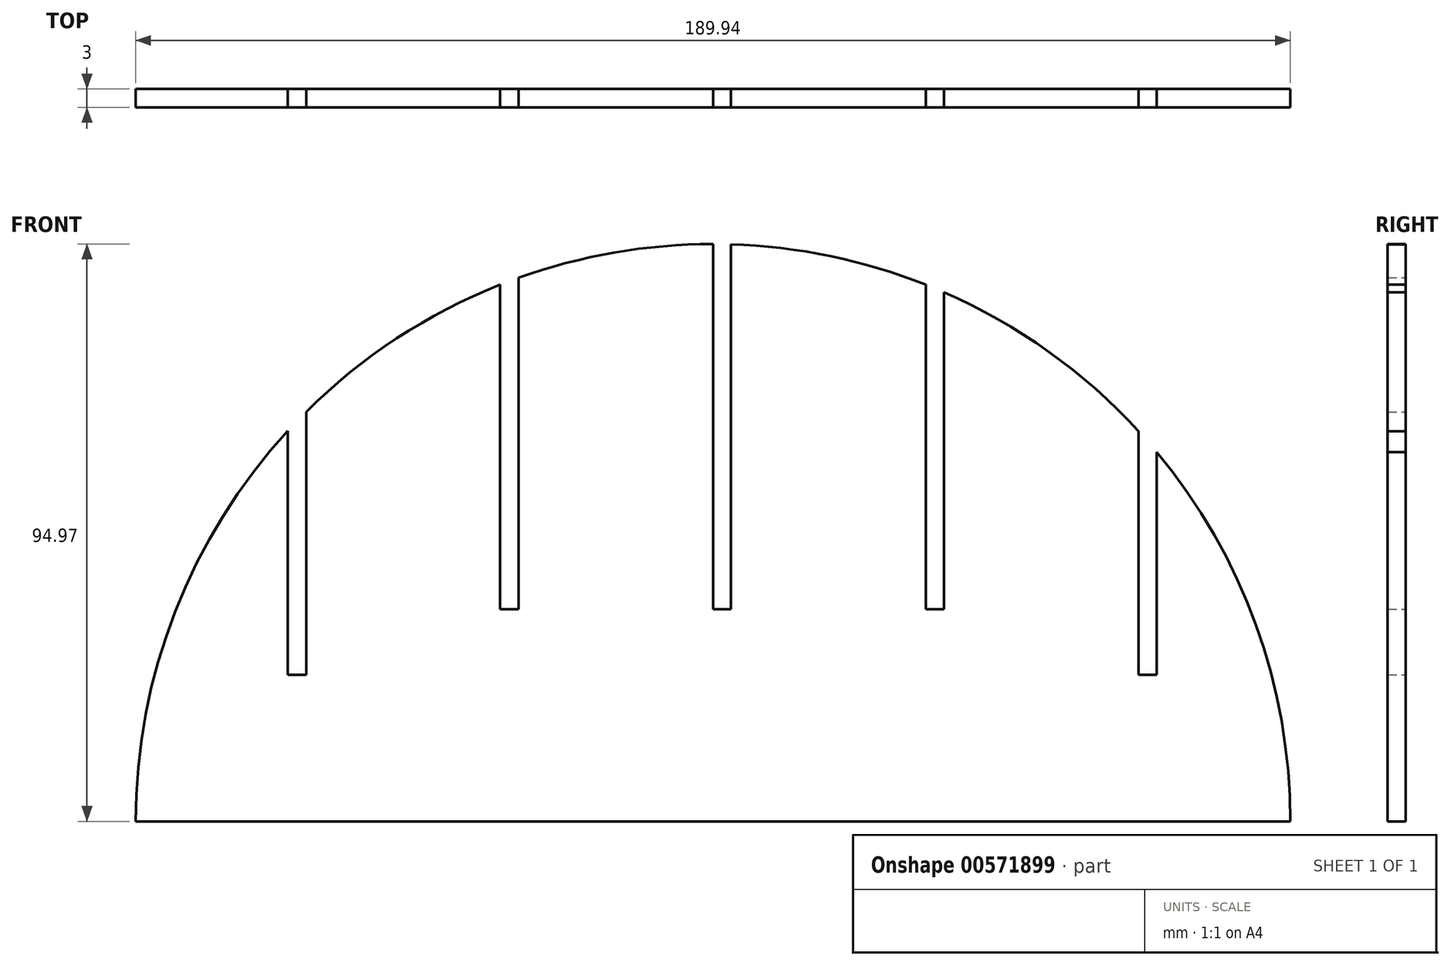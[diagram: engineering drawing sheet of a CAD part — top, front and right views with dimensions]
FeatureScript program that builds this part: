
annotation { "Feature Type Name" : "Feature", "Feature Type Description" : "" }
export const myFeature = defineFeature(function(context is Context, id is Id, definition is map)
    precondition{}
    {
        {
            var Q0;
            Q0=qCreatedBy(makeId("Front.planeOp"),FACE);
            var sketch = newSketch(context, id + "F0", { "sketchPlane" : qUnion([Q0])});
            skLineSegment(sketch, "E0", {"start": v(94.97, 0) * mm, "end": v(-95.03, 0) * mm});
            skArc(sketch, "E1", {"start": v(94.97, 0) * mm, "mid": v(89.3, 32.3) * mm, "end": v(73, 60.75) * mm});
            skLineSegment(sketch, "E2", {"start": v(-94.97, 0) * mm, "end": v(-69.93, 0) * mm});
            skLineSegment(sketch, "E3", {"start": v(94.97, 0) * mm, "end": v(70, 0) * mm});
            skLineSegment(sketch, "E4", {"start": v(-69.93, 24.1) * mm, "end": v(-69.93, 64.26) * mm});
            skLineSegment(sketch, "E5", {"start": v(-69.93, 0) * mm, "end": v(-35, 0) * mm});
            skLineSegment(sketch, "E6", {"start": v(-35, 0) * mm, "end": v(0, 0) * mm});
            skLineSegment(sketch, "E7", {"start": v(0, 0) * mm, "end": v(35, 0) * mm});
            skLineSegment(sketch, "E8", {"start": v(35, 0) * mm, "end": v(70, 0) * mm});
            skLineSegment(sketch, "E9", {"start": v(-69.93, 64.26) * mm, "end": v(-69.93, 24.1) * mm});
            skLineSegment(sketch, "E10", {"start": v(-35, 34.92) * mm, "end": v(-35, 88.28) * mm});
            skLineSegment(sketch, "E11", {"start": v(0, 34.92) * mm, "end": v(0, 94.97) * mm});
            skLineSegment(sketch, "E12", {"start": v(35, 34.92) * mm, "end": v(35, 88.28) * mm});
            skLineSegment(sketch, "E13", {"start": v(70, 24.1) * mm, "end": v(70, 64.18) * mm});
            skLineSegment(sketch, "E14", {"start": v(-35, 88.28) * mm, "end": v(-35, 34.92) * mm});
            skLineSegment(sketch, "E15", {"start": v(0, 34.92) * mm, "end": v(2.96, 34.92) * mm});
            skPoint(sketch, "E16", {"position": v(0, 34.92) * mm});
            skPoint(sketch, "E17", {"position": v(35, 34.92) * mm});
            skLineSegment(sketch, "E18", {"start": v(-69.93, 24.1) * mm, "end": v(-66.93, 24.1) * mm});
            skPoint(sketch, "E19", {"position": v(-66.93, 24.1) * mm});
            skPoint(sketch, "E20", {"position": v(-32, 34.92) * mm});
            skPoint(sketch, "E21", {"position": v(2.96, 34.92) * mm});
            skPoint(sketch, "E22", {"position": v(38, 34.92) * mm});
            skPoint(sketch, "E23", {"position": v(73, 24.1) * mm});
            skLineSegment(sketch, "E24", {"start": v(-66.93, 24.1) * mm, "end": v(-66.93, 67.38) * mm});
            skArc(sketch, "E25.trimOffspring", {"start": v(-69.93, 64.26) * mm, "mid": v(-88.49, 34.48) * mm, "end": v(-94.97, 0) * mm});
            skPoint(sketch, "E26.orphan", {"position": v(70, 24.1) * mm});
            skLineSegment(sketch, "E27", {"start": v(-32, 34.92) * mm, "end": v(-32, 89.42) * mm});
            skLineSegment(sketch, "E28", {"start": v(70, 24.1) * mm, "end": v(73, 24.1) * mm});
            skLineSegment(sketch, "E29", {"start": v(-35, 34.92) * mm, "end": v(-32, 34.92) * mm});
            skLineSegment(sketch, "E30", {"start": v(35, 34.92) * mm, "end": v(38, 34.92) * mm});
            skArc(sketch, "E31.trimOffspring", {"start": v(-35, 88.28) * mm, "mid": v(-52.03, 79.45) * mm, "end": v(-66.93, 67.38) * mm});
            skLineSegment(sketch, "E32", {"start": v(2.96, 34.92) * mm, "end": v(2.96, 94.92) * mm});
            skLineSegment(sketch, "E33", {"start": v(38, 34.92) * mm, "end": v(38, 87.04) * mm});
            skArc(sketch, "E34.trimOffspring", {"start": v(0, 94.97) * mm, "mid": v(-16.24, 93.57) * mm, "end": v(-32, 89.42) * mm});
            skArc(sketch, "E35.trimOffspring", {"start": v(35, 88.28) * mm, "mid": v(19.27, 93) * mm, "end": v(2.96, 94.92) * mm});
            skLineSegment(sketch, "E36", {"start": v(73, 24.1) * mm, "end": v(73, 60.75) * mm});
            skArc(sketch, "E37.trimOffspring", {"start": v(70, 64.18) * mm, "mid": v(55.2, 77.28) * mm, "end": v(38, 87.04) * mm});
            skSolve(sketch);
        }
        {
            var Q0;
            Q0 = qSketchRegion(id + "F0", true);
            extrude(context, id + "F1", {"entities" : qUnion([Q0]), "depth" : 3 * mm, "offsetDistance" : 25 * mm});
        }
    });
